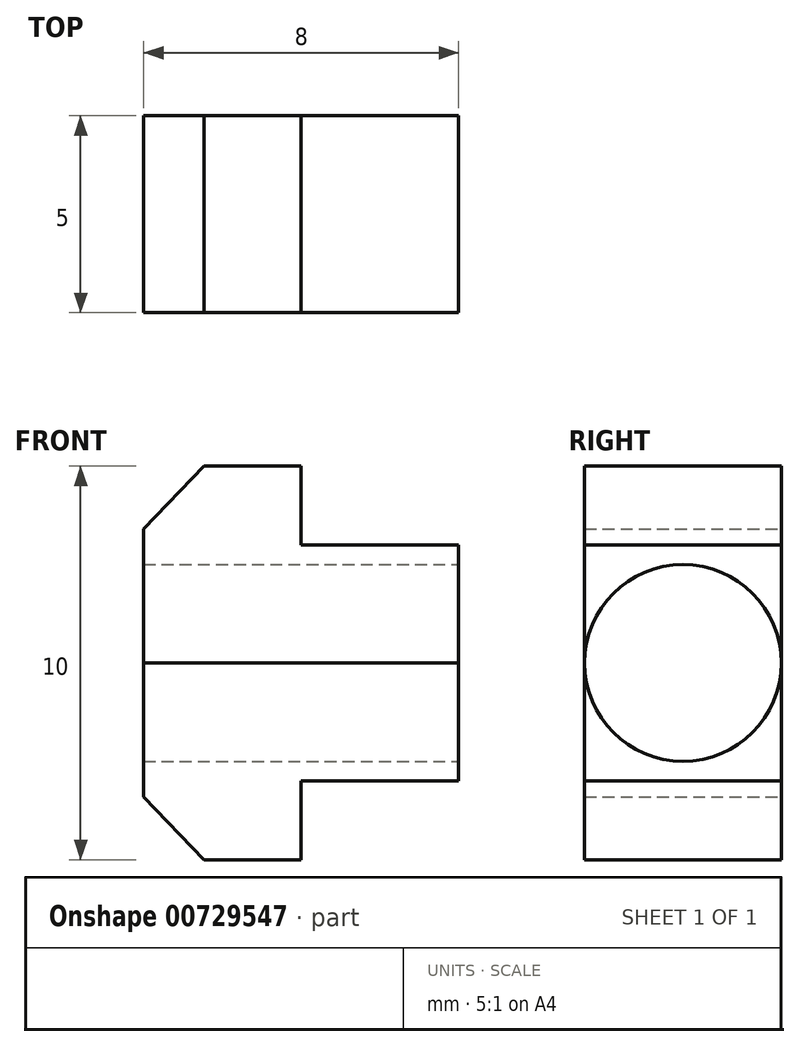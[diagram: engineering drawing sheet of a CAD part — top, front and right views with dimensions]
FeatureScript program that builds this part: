
annotation { "Feature Type Name" : "Feature", "Feature Type Description" : "" }
export const myFeature = defineFeature(function(context is Context, id is Id, definition is map)
    precondition{}
    {
        {
            var Q0;
            Q0=qCreatedBy(makeId("Front.planeOp"),FACE);
            var sketch = newSketch(context, id + "F0", { "sketchPlane" : qUnion([Q0])});
            skLineSegment(sketch, "E0", {"start": v(-58.38, 0) * mm, "end": v(-37.73, 0) * mm});
            skLineSegment(sketch, "E1", {"start": v(-52.4, 0) * mm, "end": v(-52.4, -3.4) * mm});
            skLineSegment(sketch, "E2", {"start": v(-52.4, -3.4) * mm, "end": v(-50.86, -5) * mm});
            skLineSegment(sketch, "E3", {"start": v(-50.86, -5) * mm, "end": v(-48.4, -5) * mm});
            skLineSegment(sketch, "E4", {"start": v(-48.4, -5) * mm, "end": v(-48.4, -3) * mm});
            skLineSegment(sketch, "E5", {"start": v(-48.4, -3) * mm, "end": v(-44.4, -3) * mm});
            skLineSegment(sketch, "E6", {"start": v(-44.4, -3) * mm, "end": v(-44.4, 0) * mm});
            skLineSegment(sketch, "E7", {"start": v(-52.4, 2.5) * mm, "end": v(-44.4, 2.5) * mm});
            skLineSegment(sketch, "E8.MirrorCS", {"start": v(-52.4, 0) * mm, "end": v(-52.4, 3.4) * mm});
            skLineSegment(sketch, "E9.MirrorCS", {"start": v(-52.4, -2.5) * mm, "end": v(-44.4, -2.5) * mm});
            skLineSegment(sketch, "E10.MirrorCS", {"start": v(-44.4, 3) * mm, "end": v(-44.4, 0) * mm});
            skLineSegment(sketch, "E11.MirrorCS", {"start": v(-48.4, 3) * mm, "end": v(-44.4, 3) * mm});
            skLineSegment(sketch, "E12.MirrorCS", {"start": v(-48.4, 5) * mm, "end": v(-48.4, 3) * mm});
            skLineSegment(sketch, "E13.MirrorCS", {"start": v(-50.86, 5) * mm, "end": v(-48.4, 5) * mm});
            skLineSegment(sketch, "E14.MirrorCS", {"start": v(-52.4, 3.4) * mm, "end": v(-50.86, 5) * mm});
            skLineSegment(sketch, "E15", {"start": v(15.05, 0) * mm, "end": v(23.05, 0) * mm, "construction": true});
            skLineSegment(sketch, "E16", {"start": v(15.05, 0) * mm, "end": v(15.05, -3.4) * mm});
            skLineSegment(sketch, "E17", {"start": v(15.05, -3.4) * mm, "end": v(16.65, -5) * mm});
            skLineSegment(sketch, "E18", {"start": v(16.65, -5) * mm, "end": v(19.05, -5) * mm});
            skLineSegment(sketch, "E19", {"start": v(19.05, -5) * mm, "end": v(19.05, -3) * mm});
            skLineSegment(sketch, "E20", {"start": v(19.05, -3) * mm, "end": v(23.05, -3) * mm});
            skLineSegment(sketch, "E21", {"start": v(23.05, -3) * mm, "end": v(23.05, 3) * mm});
            skLineSegment(sketch, "E22", {"start": v(15.05, 2.5) * mm, "end": v(23.05, 2.5) * mm});
            skLineSegment(sketch, "E23.MirrorCS", {"start": v(15.05, 0) * mm, "end": v(15.05, 3.4) * mm});
            skLineSegment(sketch, "E24.MirrorCS", {"start": v(15.05, -2.5) * mm, "end": v(23.05, -2.5) * mm});
            skLineSegment(sketch, "E25.MirrorCS", {"start": v(23.05, 3) * mm, "end": v(23.05, -3) * mm});
            skLineSegment(sketch, "E26.MirrorCS", {"start": v(19.05, 3) * mm, "end": v(23.05, 3) * mm});
            skLineSegment(sketch, "E27.MirrorCS", {"start": v(19.05, 5) * mm, "end": v(19.05, 3) * mm});
            skLineSegment(sketch, "E28.MirrorCS", {"start": v(16.65, 5) * mm, "end": v(19.05, 5) * mm});
            skLineSegment(sketch, "E29.MirrorCS", {"start": v(15.05, 3.4) * mm, "end": v(16.65, 5) * mm});
            skPoint(sketch, "E30.orphan", {"position": v(0, 0) * mm});
            skSolve(sketch);
        }
        {
            var Q0;
            {var subQ2=sQuery(id+"F0.wireOp",EDGE,"E7");Q0=makeQuery(id+"F0.imprint","IMPRINT",FACE,{"disambiguationData":[TD([[makeQuery(id+"F0.imprint","IMPRINT",EDGE,{"derivedFrom":subQ2}),1.0]])]});}
            var Q1;
            {var subQ3=sQuery(id+"F0.wireOp",EDGE,"E7");Q1=makeQuery(id+"F0.imprint","IMPRINT",FACE,{"disambiguationData":[TD([[makeQuery(id+"F0.imprint","IMPRINT",EDGE,{"derivedFrom":subQ3}),-1.0]])]});}
            var Q2;
            {var subQ0=sQuery(id+"F0.wireOp",EDGE,"E2");Q2=makeQuery(id+"F0.imprint","IMPRINT",FACE,{"disambiguationData":[TD([[makeQuery(id+"F0.imprint","IMPRINT",EDGE,{"derivedFrom":subQ0}),1.0]])]});}
            var Q3;
            {var subQ5=sQuery(id+"F0.wireOp",EDGE,"E9.MirrorCS");Q3=makeQuery(id+"F0.imprint","IMPRINT",FACE,{"disambiguationData":[TD([[makeQuery(id+"F0.imprint","IMPRINT",EDGE,{"derivedFrom":subQ5}),1.0]])]});}
            extrude(context, id + "F1", {"entities" : qUnion([Q0, Q1, Q2, Q3]), "depth" : 5 * mm, "offsetDistance" : 25 * mm, "symmetric" : true});
        }
        {
            var Q0;
            {var subQ5=sQuery(id+"F0.wireOp",EDGE,"E7");Q0=makeQuery(id+"F0.imprint","IMPRINT",FACE,{"disambiguationData":[TD([[makeQuery(id+"F0.imprint","IMPRINT",EDGE,{"derivedFrom":subQ5}),-1.0]])]});}
            var Q1;
            Q1=sQuery(id+"F0.wireOp",EDGE,"E0");
            revolve(context, id + "F2", {"operationType" : NewBodyOperationType.REMOVE, "surfaceOperationType" : NewSurfaceOperationType.NEW, "entities" : qUnion([Q0]), "axis" : qUnion([Q1]), "revolveType" : RevolveType.FULL, "oppositeDirection" : true});
        }
    });
